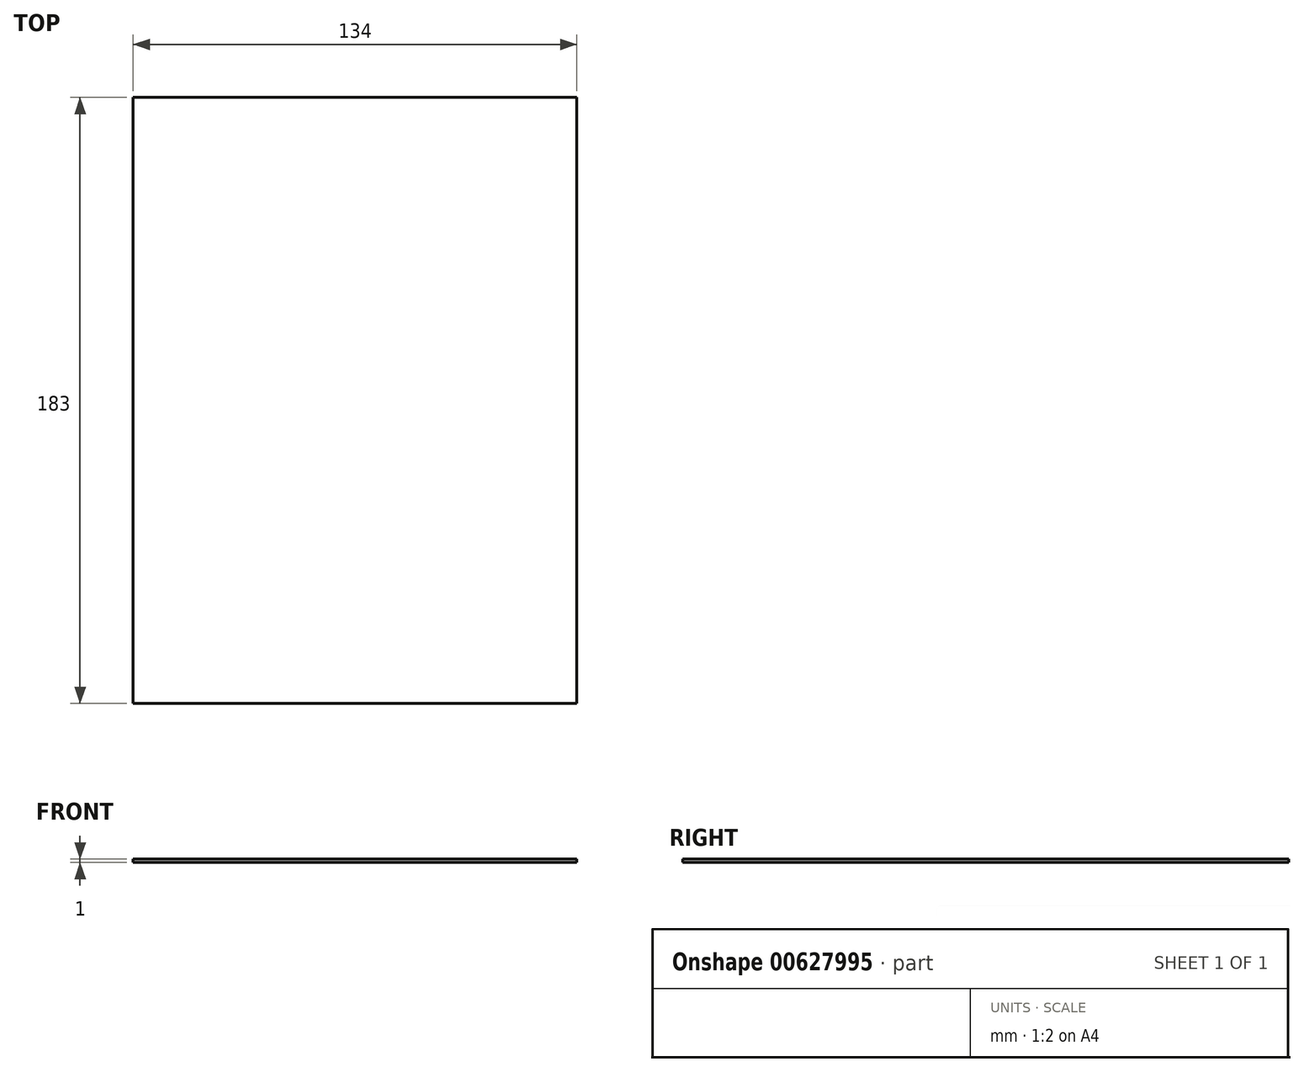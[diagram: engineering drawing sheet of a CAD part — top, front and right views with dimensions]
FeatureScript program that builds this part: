
annotation { "Feature Type Name" : "Feature", "Feature Type Description" : "" }
export const myFeature = defineFeature(function(context is Context, id is Id, definition is map)
    precondition{}
    {
        {
            var Q0;
            Q0=qCreatedBy(makeId("Top.planeOp"),FACE);
            var sketch = newSketch(context, id + "F0", { "sketchPlane" : qUnion([Q0])});
            skLineSegment(sketch, "E0.bottom", {"start": v(0, 0) * mm, "end": v(134, 0) * mm});
            skLineSegment(sketch, "E0.top", {"start": v(0, 183) * mm, "end": v(134, 183) * mm});
            skLineSegment(sketch, "E0.left", {"start": v(0, 0) * mm, "end": v(0, 183) * mm});
            skLineSegment(sketch, "E0.right", {"start": v(134, 0) * mm, "end": v(134, 183) * mm});
            skSolve(sketch);
        }
        {
            var Q0;
            Q0=qSketchRegion(id+"F0",true);
            extrude(context, id + "F1", {"entities" : qUnion([Q0]), "depth" : 1 * mm, "offsetDistance" : 25 * mm});
        }
    });
